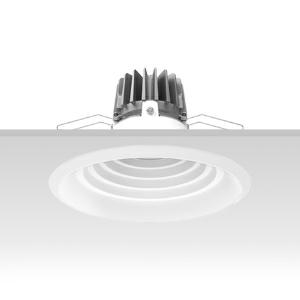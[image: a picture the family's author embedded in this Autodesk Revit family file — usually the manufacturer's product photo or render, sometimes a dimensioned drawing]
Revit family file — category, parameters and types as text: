
# Revit family: 3f_filippi_-_3f_reno_bianco_ampio_3f_filippi_-_30621_-_3f_reno_200_wh_2000-840_wide
name_source: partatom
category: Lighting Fixtures
units: mm (PartAtom-declared; Revit-internal decimal feet)

## family parameters
Cut with Voids When Loaded = No
Host = Face
Light Source = No
Part Type = Normal
Room Calculation Point = No
Round Connector Dimension = Use Diameter
Shared = No

## types (1)
- 3F Filippi - 3F Reno Bianco Ampio (1 x LED, 1963 lm, 20 W, 4000 K)
    Apparent Load = 20 VA
    Approval mark = CE
    CIE Flux Codes = 80 97 100 100 100
    Color Rendering = 80
    Color Temperature = 4000 K
    Control Gear = Electronic ballast
    Default Elevation = 1800 mm
    Description = ILLUMINOTECHNICAL
Luminous efficiency 100% (DLOR 100%, ULOR 0%).
Initial luminous flux of the luminaire 1963 lm.
Direct symmetric wide distribution.
Installation Interdistance Transv.D = 1.56 x hu - Long.D = 1.56 x hu.
Average luminance <3000 cd/m² for radial angles >65°.
Tabular UGR (CIE 117 - 4H-8H; S=0.25H; 70/50/20): RUG 19.3 - 19.4.
Beam angle: 85° - 84°.
Luminous efficacy 98 lm/W.
Lifetime (L90/B10): 30000 h. (tq+25°C)
Lifetime (L85/B10): 50000 h. (tq+25°C)
Lifetime (L70/B10): 80000 h. (tq+25°C)
Sudden decreased luminous flux after 50000 hours: 0% (C0).
Photobiological safety in compliance with IEC/TR 62778: RG0 risk exempt, (IEC 62471).
In compliance with IEC/EN 62722-2-1 - IEC/EN 62717 standards.

SOURCE
Compact LED module 2000/840.
Energy efficiency class (UE 2019/2020 - UE 2019/2015): D.
CIE 13.3 Colour rendering index: CRI >80 (R9 <50%).
IES TM-30 Fidelity Index: Rf = 84 Rg = 95.
CCT nominal colour temperature 4000 K.
Colour initial tolerance (MacAdam): SDCM 3.
Zhaga Book 3 compliant.

MECHANICAL
Passive heat dissipator in die-casting aluminium, oversized, for optimum thermal management of the LED module.
Parabolic element with graduated/concentric rings in white polycarbonate.
Transparent external lens with glossy and satin differentiated surfaces, with a cooling and anti-insect system in methacrylate (PMMA).
Fastening spring clips in stainless steel.
Dimensions: diameter 216 mm, height 142 mm. Weight 0.8 kg.
IP44 protection degree for exposed part, IP20 for recessed part.
Mechanical strength to impacts IK04 (0.5 joule).
Glow-wire test resistance 650°C.

ELECTRICAL
Wiring on a separate unit.
Halogen Free electronic wiring 230V-50/60Hz, power factor 0.95, THD <25%, constant output current, SELV, class II, 1 driver.
Power of the luminaire 20 W.
ENEC - CE.
SAFE FLICKER: PstLM=<1 and SVM=<0.4 (IEC TR 61547-1 and IEC TR 63158), to ensure a more comfortable and safe light.
Luminaire compliant with EN 60598-2-22 for power supply from a centralised emergency system CPSS (Central Power Supply System), not incorporated in the luminaire - high risk areas excluded. The default power and flux are 100% in AC and 100% in DC.
Ambient temperature from 0°C to +25°C.
Temperature class T6 max 85°C.
Relative humidity UR: <85%.

INSTALLATION
Pull-up recessed fitting.
False ceiling carving: 200 mm.
All accessories dedicated to this product are available on the Catalog and on our website www.3F-Filippi.com.

APPLICATIONS
Environments: architectural, commercial, exhibition areas, transit areas, corridors, shops, display windows, service areas.
In false ceilings with narrow voids.

WARNING
Luminaire designed for disposal/recycling at end-of-life.
Replaceable (LED only) light source by a professional. Replaceable control gear by a professional.
    Height = 0 mm  [stored 0 ft]
    Lamp = 1 x LED
    Lamp Light Flux = 1963 lm
    Lamp Power = 20 W
    Lamp count = 1
    Length = 216 mm
    Lifetime = 50000 h
    Luminous efficacy = 98 lm/W
    Manufacturer = 3F Filippi
    ModVariant = No
    Model = 3F Filippi - 30621 - 3F Reno 200 WH 2000-840 WIDE
    Mounting Place = Ceiling
    Mounting Type = Recessed
    Number of Poles = 1
    OnlyDefault = Yes
    Power Factor = 1
    Product Name = 3F Filippi - 3F Reno Bianco Ampio
    Product group = recessed luminaire
    ProductGroupID = 4
    Protection Class = Protection class II
    Protection Degree = IP 20
    RLX_Detail_Level = 1
    RLX_Emergency_Light_Flux = 0 lm
    RLX_Emergency_Type = 0
    RLX_Emergency_Type_DB = No
    RlxData = <blob elided: 87521 chars, md5=56184d4c>
    Socket = socket
    Standby Power = 0 W
    System Light Flux = 1963 lm
    System Power = 20 W
    Type Comments = Product without accessories
    Type Image = 3ffilippi_3f_reno_200_wh_2000.jpg
    URL = http://relux.com
    VarID = ---
    Voltage = 0 V
    Weight = 0.00 kg
    Width = 0 mm  [stored 0 ft]

note: [stored X ft] marks values corroborated as IEEE doubles in the binary element streams (Revit-internal decimal feet)

## geometry (parser evidence)
native form markers: Blend x4, Sweep x11
no freeform markers — native parametric forms only
